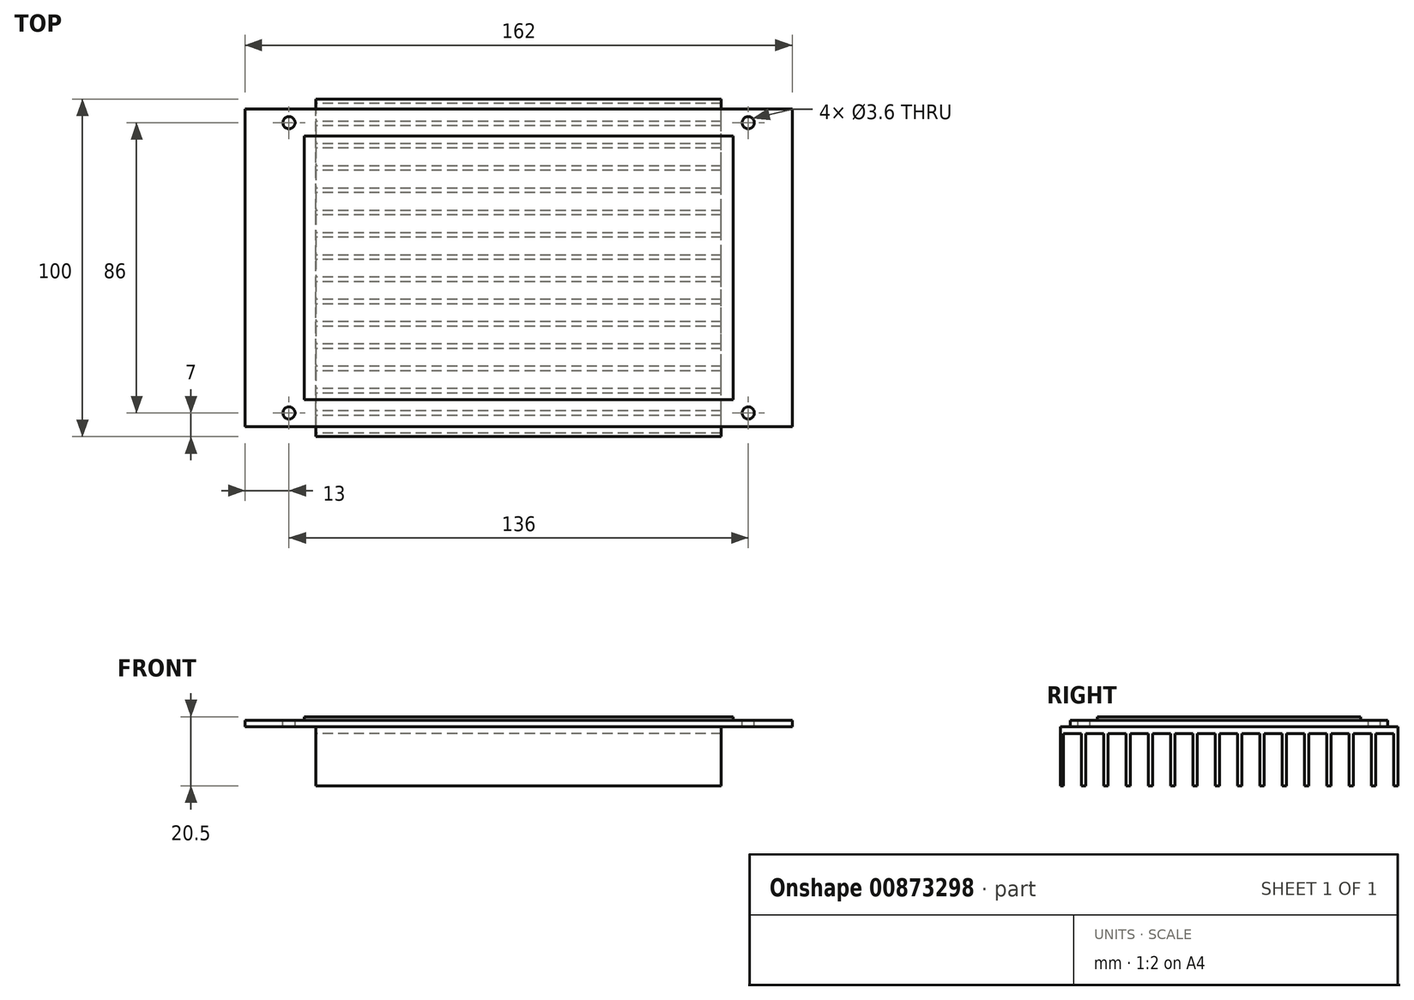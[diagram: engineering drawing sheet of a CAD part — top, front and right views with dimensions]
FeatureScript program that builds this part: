
annotation { "Feature Type Name" : "Feature", "Feature Type Description" : "" }
export const myFeature = defineFeature(function(context is Context, id is Id, definition is map)
    precondition{}
    {
        {
            var Q0;
            Q0=qCreatedBy(makeId("Top.planeOp"),FACE);
            var sketch = newSketch(context, id + "F0", { "sketchPlane" : qUnion([Q0])});
            skLineSegment(sketch, "E0.bottom", {"start": v(0, 0) * mm, "end": v(162, 0) * mm});
            skLineSegment(sketch, "E0.top", {"start": v(0, 94) * mm, "end": v(162, 94) * mm});
            skLineSegment(sketch, "E0.left", {"start": v(0, 0) * mm, "end": v(0, 94) * mm});
            skLineSegment(sketch, "E0.right", {"start": v(162, 0) * mm, "end": v(162, 94) * mm});
            skLineSegment(sketch, "E1", {"start": v(0, 47) * mm, "end": v(162, 47) * mm, "construction": true});
            skLineSegment(sketch, "E2", {"start": v(81, 94) * mm, "end": v(81, 0) * mm, "construction": true});
            skLineSegment(sketch, "E3.bottom", {"start": v(144.5, 86) * mm, "end": v(17.5, 86) * mm});
            skLineSegment(sketch, "E3.top", {"start": v(144.5, 8) * mm, "end": v(17.5, 8) * mm});
            skLineSegment(sketch, "E3.left", {"start": v(144.5, 86) * mm, "end": v(144.5, 8) * mm});
            skLineSegment(sketch, "E3.right", {"start": v(17.5, 86) * mm, "end": v(17.5, 8) * mm});
            skPoint(sketch, "E3.middle", {"position": v(81, 47) * mm});
            skLineSegment(sketch, "E4.bottom", {"start": v(149, 90) * mm, "end": v(13, 90) * mm, "construction": true});
            skLineSegment(sketch, "E4.top", {"start": v(149, 4) * mm, "end": v(13, 4) * mm, "construction": true});
            skLineSegment(sketch, "E4.left", {"start": v(149, 90) * mm, "end": v(149, 4) * mm, "construction": true});
            skLineSegment(sketch, "E4.right", {"start": v(13, 90) * mm, "end": v(13, 4) * mm, "construction": true});
            skCircle(sketch, "E5", {"center": v(149, 90) * mm, "radius": 1.8 * mm});
            skCircle(sketch, "E6.MirrorC", {"center": v(13, 90) * mm, "radius": 1.8 * mm});
            skCircle(sketch, "E7.MirrorC", {"center": v(149, 4) * mm, "radius": 1.8 * mm});
            skCircle(sketch, "E8.MirrorC", {"center": v(13, 4) * mm, "radius": 1.8 * mm});
            skSolve(sketch);
        }
        {
            var Q0;
            Q0=makeQuery(id+"F0.imprint","IMPRINT",FACE,{"disambiguationData":[TD([[makeQuery(id+"F0.imprint","IMPRINT",EDGE,{"derivedFrom":sQuery(id+"F0.wireOp",EDGE,"E0.bottom")}),1.0]])]});
            var Q1;
            Q1=makeQuery(id+"F0.imprint","IMPRINT",FACE,{"disambiguationData":[TD([[makeQuery(id+"F0.imprint","IMPRINT",EDGE,{"derivedFrom":sQuery(id+"F0.wireOp",EDGE,"E3.bottom")}),1.0]])]});
            extrude(context, id + "F1", {"entities" : qUnion([Q0, Q1]), "oppositeDirection" : true, "depth" : 2 * mm, "offsetDistance" : 25 * mm});
        }
        {
            var Q0;
            Q0=makeQuery(id+"F0.imprint","IMPRINT",FACE,{"disambiguationData":[TD([[makeQuery(id+"F0.imprint","IMPRINT",EDGE,{"derivedFrom":sQuery(id+"F0.wireOp",EDGE,"E3.bottom")}),1.0]])]});
            extrude(context, id + "F2", {"entities" : qUnion([Q0]), "depth" : 1 * mm, "offsetDistance" : 25 * mm});
        }
        {
            var Q0;
            Q0=makeQuery(id+"F1.opExtrude","CAP_FACE",FACE,{"disambiguationData":[OSD([sQuery(id+"F0.wireOp",EDGE,"E0.bottom"),sQuery(id+"F0.wireOp",EDGE,"E0.top"),sQuery(id+"F0.wireOp",EDGE,"E0.left"),sQuery(id+"F0.wireOp",EDGE,"E0.right")])],"isStart":false});
            var sketch = newSketch(context, id + "F3", { "sketchPlane" : qUnion([Q0])});
            skLineSegment(sketch, "E9.0", {"start": v(81, -94) * mm, "end": v(81, 0) * mm, "construction": true});
            skLineSegment(sketch, "E9.1", {"start": v(0, -47) * mm, "end": v(162, -47) * mm, "construction": true});
            skLineSegment(sketch, "E10.bottom", {"start": v(141, 3) * mm, "end": v(21, 3) * mm});
            skLineSegment(sketch, "E10.top", {"start": v(141, -97) * mm, "end": v(21, -97) * mm});
            skLineSegment(sketch, "E10.left", {"start": v(141, 3) * mm, "end": v(141, -97) * mm});
            skLineSegment(sketch, "E10.right", {"start": v(21, 3) * mm, "end": v(21, -97) * mm});
            skPoint(sketch, "E10.middle", {"position": v(81, -47) * mm});
            skSolve(sketch);
        }
        {
            var Q0;
            Q0 = qSketchRegion(id + "F3", true);
            extrude(context, id + "F4", {"entities" : qUnion([Q0]), "depth" : 17.5 * mm, "offsetDistance" : 25 * mm});
        }
        {
            var Q0;
            Q0=makeQuery(id+"F4.opExtrude","SWEPT_FACE",FACE,{"disambiguationData":[OSD([sQuery(id+"F3.wireOp",EDGE,"E10.right")])]});
            var sketch = newSketch(context, id + "F5", { "sketchPlane" : qUnion([Q0])});
            skLineSegment(sketch, "E11.bottom", {"start": v(-95.7, -19.5) * mm, "end": v(-90.4, -19.5) * mm});
            skLineSegment(sketch, "E11.top", {"start": v(-95.7, -4) * mm, "end": v(-90.4, -4) * mm});
            skLineSegment(sketch, "E11.left", {"start": v(-95.7, -19.5) * mm, "end": v(-95.7, -4) * mm});
            skLineSegment(sketch, "E11.right", {"start": v(-90.4, -19.5) * mm, "end": v(-90.4, -4) * mm});
            skLineSegment(sketch, "E12.1.0.0", {"start": v(-89.1, -19.5) * mm, "end": v(-89.1, -4) * mm});
            skLineSegment(sketch, "E12.1.0.1", {"start": v(-83.8, -19.5) * mm, "end": v(-83.8, -4) * mm});
            skLineSegment(sketch, "E12.1.0.2", {"start": v(-89.1, -19.5) * mm, "end": v(-83.8, -19.5) * mm});
            skLineSegment(sketch, "E12.1.0.3", {"start": v(-89.1, -4) * mm, "end": v(-83.8, -4) * mm});
            skLineSegment(sketch, "E12.2.0.0", {"start": v(-82.5, -19.5) * mm, "end": v(-82.5, -4) * mm});
            skLineSegment(sketch, "E12.2.0.1", {"start": v(-77.2, -19.5) * mm, "end": v(-77.2, -4) * mm});
            skLineSegment(sketch, "E12.2.0.2", {"start": v(-82.5, -19.5) * mm, "end": v(-77.2, -19.5) * mm});
            skLineSegment(sketch, "E12.2.0.3", {"start": v(-82.5, -4) * mm, "end": v(-77.2, -4) * mm});
            skLineSegment(sketch, "E12.3.0.0", {"start": v(-75.9, -19.5) * mm, "end": v(-75.9, -4) * mm});
            skLineSegment(sketch, "E12.3.0.1", {"start": v(-70.6, -19.5) * mm, "end": v(-70.6, -4) * mm});
            skLineSegment(sketch, "E12.3.0.2", {"start": v(-75.9, -19.5) * mm, "end": v(-70.6, -19.5) * mm});
            skLineSegment(sketch, "E12.3.0.3", {"start": v(-75.9, -4) * mm, "end": v(-70.6, -4) * mm});
            skLineSegment(sketch, "E12.4.0.0", {"start": v(-69.3, -19.5) * mm, "end": v(-69.3, -4) * mm});
            skLineSegment(sketch, "E12.4.0.1", {"start": v(-64, -19.5) * mm, "end": v(-64, -4) * mm});
            skLineSegment(sketch, "E12.4.0.2", {"start": v(-69.3, -19.5) * mm, "end": v(-64, -19.5) * mm});
            skLineSegment(sketch, "E12.4.0.3", {"start": v(-69.3, -4) * mm, "end": v(-64, -4) * mm});
            skLineSegment(sketch, "E12.5.0.0", {"start": v(-62.7, -19.5) * mm, "end": v(-62.7, -4) * mm});
            skLineSegment(sketch, "E12.5.0.1", {"start": v(-57.4, -19.5) * mm, "end": v(-57.4, -4) * mm});
            skLineSegment(sketch, "E12.5.0.2", {"start": v(-62.7, -19.5) * mm, "end": v(-57.4, -19.5) * mm});
            skLineSegment(sketch, "E12.5.0.3", {"start": v(-62.7, -4) * mm, "end": v(-57.4, -4) * mm});
            skLineSegment(sketch, "E12.6.0.0", {"start": v(-56.1, -19.5) * mm, "end": v(-56.1, -4) * mm});
            skLineSegment(sketch, "E12.6.0.1", {"start": v(-50.8, -19.5) * mm, "end": v(-50.8, -4) * mm});
            skLineSegment(sketch, "E12.6.0.2", {"start": v(-56.1, -19.5) * mm, "end": v(-50.8, -19.5) * mm});
            skLineSegment(sketch, "E12.6.0.3", {"start": v(-56.1, -4) * mm, "end": v(-50.8, -4) * mm});
            skLineSegment(sketch, "E12.7.0.0", {"start": v(-49.5, -19.5) * mm, "end": v(-49.5, -4) * mm});
            skLineSegment(sketch, "E12.7.0.1", {"start": v(-44.2, -19.5) * mm, "end": v(-44.2, -4) * mm});
            skLineSegment(sketch, "E12.7.0.2", {"start": v(-49.5, -19.5) * mm, "end": v(-44.2, -19.5) * mm});
            skLineSegment(sketch, "E12.7.0.3", {"start": v(-49.5, -4) * mm, "end": v(-44.2, -4) * mm});
            skLineSegment(sketch, "E12.8.0.0", {"start": v(-42.9, -19.5) * mm, "end": v(-42.9, -4) * mm});
            skLineSegment(sketch, "E12.8.0.1", {"start": v(-37.6, -19.5) * mm, "end": v(-37.6, -4) * mm});
            skLineSegment(sketch, "E12.8.0.2", {"start": v(-42.9, -19.5) * mm, "end": v(-37.6, -19.5) * mm});
            skLineSegment(sketch, "E12.8.0.3", {"start": v(-42.9, -4) * mm, "end": v(-37.6, -4) * mm});
            skLineSegment(sketch, "E12.9.0.0", {"start": v(-36.3, -19.5) * mm, "end": v(-36.3, -4) * mm});
            skLineSegment(sketch, "E12.9.0.1", {"start": v(-31, -19.5) * mm, "end": v(-31, -4) * mm});
            skLineSegment(sketch, "E12.9.0.2", {"start": v(-36.3, -19.5) * mm, "end": v(-31, -19.5) * mm});
            skLineSegment(sketch, "E12.9.0.3", {"start": v(-36.3, -4) * mm, "end": v(-31, -4) * mm});
            skLineSegment(sketch, "E12.10.0.0", {"start": v(-29.7, -19.5) * mm, "end": v(-29.7, -4) * mm});
            skLineSegment(sketch, "E12.10.0.1", {"start": v(-24.4, -19.5) * mm, "end": v(-24.4, -4) * mm});
            skLineSegment(sketch, "E12.10.0.2", {"start": v(-29.7, -19.5) * mm, "end": v(-24.4, -19.5) * mm});
            skLineSegment(sketch, "E12.10.0.3", {"start": v(-29.7, -4) * mm, "end": v(-24.4, -4) * mm});
            skLineSegment(sketch, "E12.11.0.0", {"start": v(-23.1, -19.5) * mm, "end": v(-23.1, -4) * mm});
            skLineSegment(sketch, "E12.11.0.1", {"start": v(-17.8, -19.5) * mm, "end": v(-17.8, -4) * mm});
            skLineSegment(sketch, "E12.11.0.2", {"start": v(-23.1, -19.5) * mm, "end": v(-17.8, -19.5) * mm});
            skLineSegment(sketch, "E12.11.0.3", {"start": v(-23.1, -4) * mm, "end": v(-17.8, -4) * mm});
            skLineSegment(sketch, "E12.12.0.0", {"start": v(-16.5, -19.5) * mm, "end": v(-16.5, -4) * mm});
            skLineSegment(sketch, "E12.12.0.1", {"start": v(-11.2, -19.5) * mm, "end": v(-11.2, -4) * mm});
            skLineSegment(sketch, "E12.12.0.2", {"start": v(-16.5, -19.5) * mm, "end": v(-11.2, -19.5) * mm});
            skLineSegment(sketch, "E12.12.0.3", {"start": v(-16.5, -4) * mm, "end": v(-11.2, -4) * mm});
            skLineSegment(sketch, "E12.13.0.0", {"start": v(-9.9, -19.5) * mm, "end": v(-9.9, -4) * mm});
            skLineSegment(sketch, "E12.13.0.1", {"start": v(-4.6, -19.5) * mm, "end": v(-4.6, -4) * mm});
            skLineSegment(sketch, "E12.13.0.2", {"start": v(-9.9, -19.5) * mm, "end": v(-4.6, -19.5) * mm});
            skLineSegment(sketch, "E12.13.0.3", {"start": v(-9.9, -4) * mm, "end": v(-4.6, -4) * mm});
            skLineSegment(sketch, "E12.14.0.0", {"start": v(-3.3, -19.5) * mm, "end": v(-3.3, -4) * mm});
            skLineSegment(sketch, "E12.14.0.1", {"start": v(2, -19.5) * mm, "end": v(2, -4) * mm});
            skLineSegment(sketch, "E12.14.0.2", {"start": v(-3.3, -19.5) * mm, "end": v(2, -19.5) * mm});
            skLineSegment(sketch, "E12.14.0.3", {"start": v(-3.3, -4) * mm, "end": v(2, -4) * mm});
            skLineSegment(sketch, "E12.direction1", {"start": v(-95.7, -19.5) * mm, "end": v(-89.1, -19.5) * mm, "construction": true});
            skSolve(sketch);
        }
        {
            var Q0;
            Q0 = qSketchRegion(id + "F5", true);
            extrude(context, id + "F6", {"entities" : qUnion([Q0]), "operationType" : NewBodyOperationType.REMOVE, "endBound" : BoundingType.THROUGH_ALL, "oppositeDirection" : true, "depth" : 25 * mm, "offsetDistance" : 25 * mm});
        }
    });
